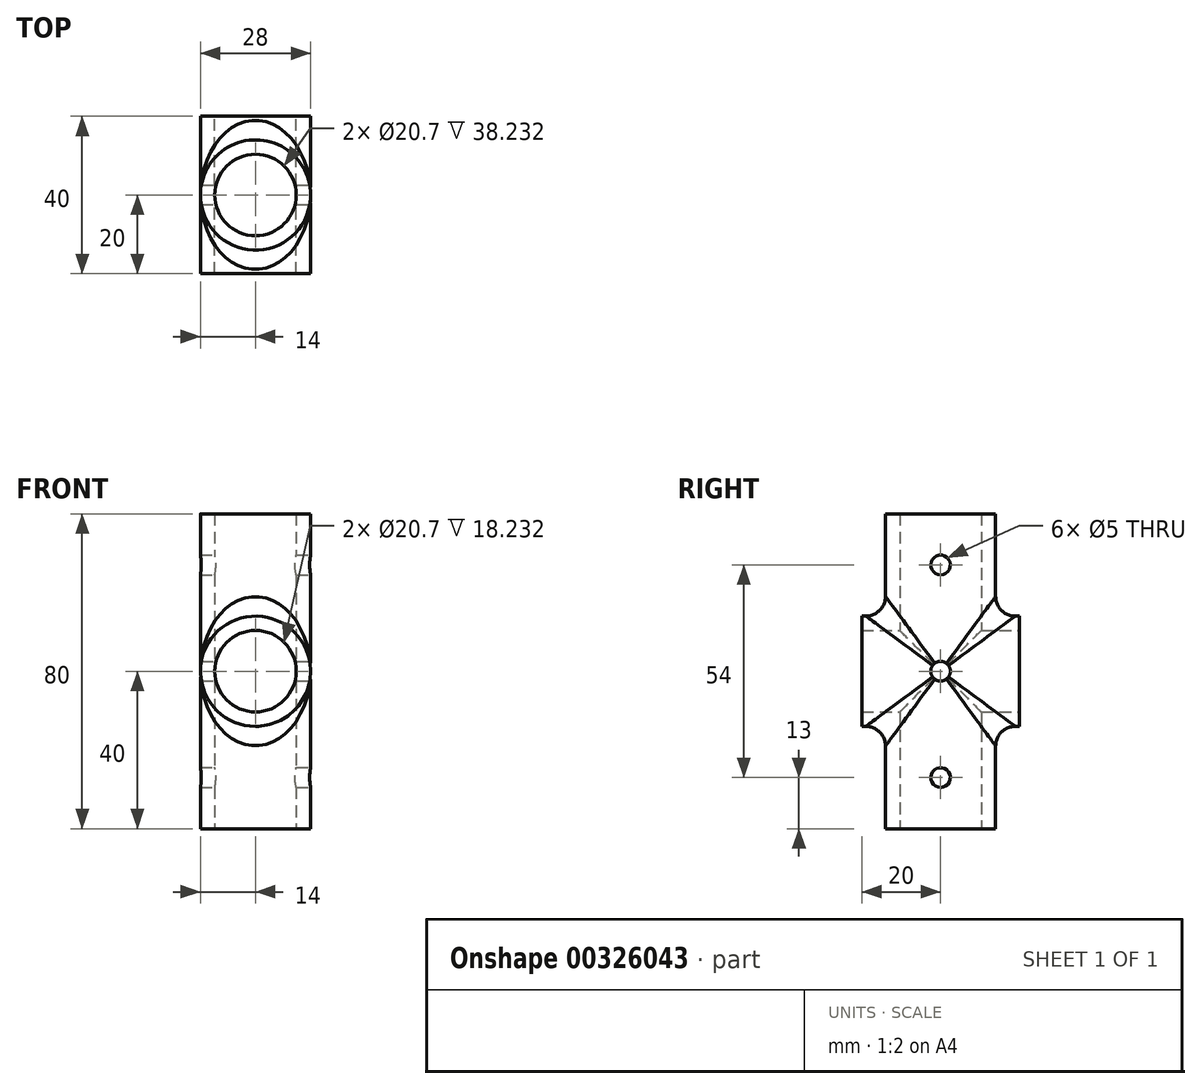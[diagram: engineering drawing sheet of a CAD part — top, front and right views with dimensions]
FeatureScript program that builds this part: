
annotation { "Feature Type Name" : "Feature", "Feature Type Description" : "" }
export const myFeature = defineFeature(function(context is Context, id is Id, definition is map)
    precondition{}
    {
        {
            var Q0;
            Q0=qCreatedBy(makeId("Front.planeOp"),FACE);
            var sketch = newSketch(context, id + "F0", { "sketchPlane" : qUnion([Q0])});
            skCircle(sketch, "E0", {"center": v(0, 0) * mm, "radius": 14 * mm});
            skSolve(sketch);
        }
        {
            var Q0;
            Q0=makeQuery(id+"F0.imprint","IMPRINT",FACE,{"disambiguationData":[TD([[makeQuery(id+"F0.imprint","IMPRINT",EDGE,{"derivedFrom":sQuery(id+"F0.wireOp",EDGE,"E0")}),1.0]])]});
            extrude(context, id + "F1", {"entities" : qUnion([Q0]), "depth" : 20 * mm, "hasSecondDirection" : true, "secondDirectionOppositeDirection" : true, "secondDirectionDepth" : 20 * mm});
        }
        {
            var Q0;
            Q0=qCreatedBy(makeId("Top.planeOp"),FACE);
            var sketch = newSketch(context, id + "F2", { "sketchPlane" : qUnion([Q0])});
            skCircle(sketch, "E1", {"center": v(0, 0) * mm, "radius": 14 * mm});
            skSolve(sketch);
        }
        {
            var Q0;
            Q0=makeQuery(id+"F2.imprint","IMPRINT",FACE,{"disambiguationData":[TD([[makeQuery(id+"F2.imprint","IMPRINT",EDGE,{"derivedFrom":sQuery(id+"F2.wireOp",EDGE,"E1")}),1.0]])]});
            extrude(context, id + "F3", {"entities" : qUnion([Q0]), "operationType" : NewBodyOperationType.ADD, "depth" : 40 * mm, "hasSecondDirection" : true, "secondDirectionOppositeDirection" : true, "secondDirectionDepth" : 40 * mm});
        }
        {
            var Q0;
            Q0=makeQuery(id+"F1.opExtrude","CAP_FACE",FACE,{"disambiguationData":[OSD([sQuery(id+"F0.wireOp",EDGE,"E0")])],"isStart":false});
            var sketch = newSketch(context, id + "F4", { "sketchPlane" : qUnion([Q0])});
            skPoint(sketch, "E2.0", {"position": v(0, 0) * mm});
            skSolve(sketch);
        }
        {
            var Q0;
            Q0=makeQuery(id+"F3.opExtrude","CAP_FACE",FACE,{"disambiguationData":[OSD([sQuery(id+"F2.wireOp",EDGE,"E1")])],"isStart":false});
            var sketch = newSketch(context, id + "F5", { "sketchPlane" : qUnion([Q0])});
            skPoint(sketch, "E3.0", {"position": v(0, 0) * mm});
            skSolve(sketch);
        }
        {
            var Q0;
            Q0=sQuery(id+"F4.wireOp",VERTEX,"E2.0");
            var Q1;
            Q1=sQuery(id+"F5.wireOp",VERTEX,"E3.0");
            var Q2;
            Q2=makeQuery(id+"F1.opExtrude","SWEPT_BODY",BODY,{"disambiguationData":[OSD([sQuery(id+"F0.wireOp",EDGE,"E0")])]});
            hole(context, id + "F6", {"style" : HoleStyle.SIMPLE, "endStyle" : HoleEndStyle.BLIND, "holeDiameter" : 20.7 * mm, "holeDepth" : 80 * mm, "tappedDepth" : 12 * mm, "tapClearance" : 3, "locations" : qUnion([Q0, Q1]), "scope" : qUnion([Q2]), "startStyle" : HoleStartStyle.PART});
        }
        {
            var Q0;
            Q0=makeQuery(id+"FaHmLC6Gn3Dgabr_1.boolean.opBoolean","INTERSECT",EDGE,{"derivedFrom":[makeQuery(id+"F3.opExtrude","SWEPT_FACE",FACE,{"disambiguationData":[OSD([sQuery(id+"F2.wireOp",EDGE,"E1")])]}),makeQuery(id+"FaHmLC6Gn3Dgabr_1.opExtrude","SWEPT_FACE",FACE,{"disambiguationData":[OSD([sQuery(id+"FM3x9xQwSGay4u9_1.wireOp",EDGE,"9ACyZtps-vr8r-rKMI-yhLd-u2BAxOoJ523N")])]})]});
            var Q1;
            Q1=makeQuery(id+"FaHmLC6Gn3Dgabr_1.boolean.opBoolean","INTERSECT",EDGE,{"derivedFrom":[makeQuery(id+"F1.opExtrude","SWEPT_FACE",FACE,{"disambiguationData":[OSD([sQuery(id+"F0.wireOp",EDGE,"E0")])]}),makeQuery(id+"FaHmLC6Gn3Dgabr_1.opExtrude","SWEPT_FACE",FACE,{"disambiguationData":[OSD([sQuery(id+"FM3x9xQwSGay4u9_1.wireOp",EDGE,"9ACyZtps-vr8r-rKMI-yhLd-u2BAxOoJ523N")])]})]});
            var Q2;
            Q2=makeQuery(id+"F3.boolean.opBoolean","INTERSECT",EDGE,{"derivedFrom":[makeQuery(id+"F1.opExtrude","SWEPT_FACE",FACE,{"disambiguationData":[OSD([sQuery(id+"F0.wireOp",EDGE,"E0")])]}),makeQuery(id+"F3.opExtrude","SWEPT_FACE",FACE,{"disambiguationData":[OSD([sQuery(id+"F2.wireOp",EDGE,"E1")])]})]});
            fillet(context, id + "F7", {"entities" : qUnion([Q0, Q1, Q2]), "radius" : 5 * mm, "tangentPropagation" : true, "allowEdgeOverflow" : false});
        }
        {
            var Q0;
            Q0=qCreatedBy(makeId("Right.planeOp"),FACE);
            cPlane(context, id + "F8", {"entities" : qUnion([Q0]), "cplaneType" : CPlaneType.OFFSET, "offset" : 25 * mm, "oppositeDirection" : true, "width" : 150 * mm, "height" : 150 * mm});
        }
        {
            var Q0;
            Q0=qCreatedBy(id+"F8.planeOp",FACE);
            var sketch = newSketch(context, id + "F9", { "sketchPlane" : qUnion([Q0])});
            skLineSegment(sketch, "E4.0", {"start": v(-14, 40) * mm, "end": v(14, 40) * mm});
            skLineSegment(sketch, "E5.0", {"start": v(-20, -14) * mm, "end": v(-20, 14) * mm});
            skPoint(sketch, "E6", {"position": v(0, 27) * mm});
            skPoint(sketch, "E6.positionSnap0", {"position": v(0, 40) * mm});
            skPoint(sketch, "E7", {"position": v(0, 0) * mm});
            skPoint(sketch, "E7.positionSnap0", {"position": v(-20, 0) * mm});
            skCircle(sketch, "E8.0", {"center": v(0, 0) * mm, "radius": 14 * mm, "construction": true});
            skLineSegment(sketch, "E9", {"start": v(0, 40) * mm, "end": v(0, 14) * mm, "construction": true});
            skLineSegment(sketch, "E10.0", {"start": v(-14, -40) * mm, "end": v(14, -40) * mm});
            skLineSegment(sketch, "E11", {"start": v(0, -40) * mm, "end": v(0, -14) * mm, "construction": true});
            skPoint(sketch, "E12", {"position": v(0, -27) * mm});
            skSolve(sketch);
        }
        {
            var Q0;
            Q0=sQuery(id+"F9.wireOp",VERTEX,"E6");
            var Q1;
            Q1=sQuery(id+"F9.wireOp",VERTEX,"E7");
            var Q2;
            Q2=sQuery(id+"F9.wireOp",VERTEX,"E12");
            var Q3;
            Q3=makeQuery(id+"F1.opExtrude","SWEPT_BODY",BODY,{"disambiguationData":[OSD([sQuery(id+"F0.wireOp",EDGE,"E0")])]});
            hole(context, id + "F10", {"style" : HoleStyle.SIMPLE, "endStyle" : HoleEndStyle.BLIND, "oppositeDirection" : true, "holeDiameter" : 5 * mm, "holeDepth" : 30 * mm, "tappedDepth" : 12 * mm, "tapClearance" : 3, "locations" : qUnion([Q0, Q1, Q2]), "scope" : qUnion([Q3]), "startStyle" : HoleStartStyle.PART});
        }
    });
